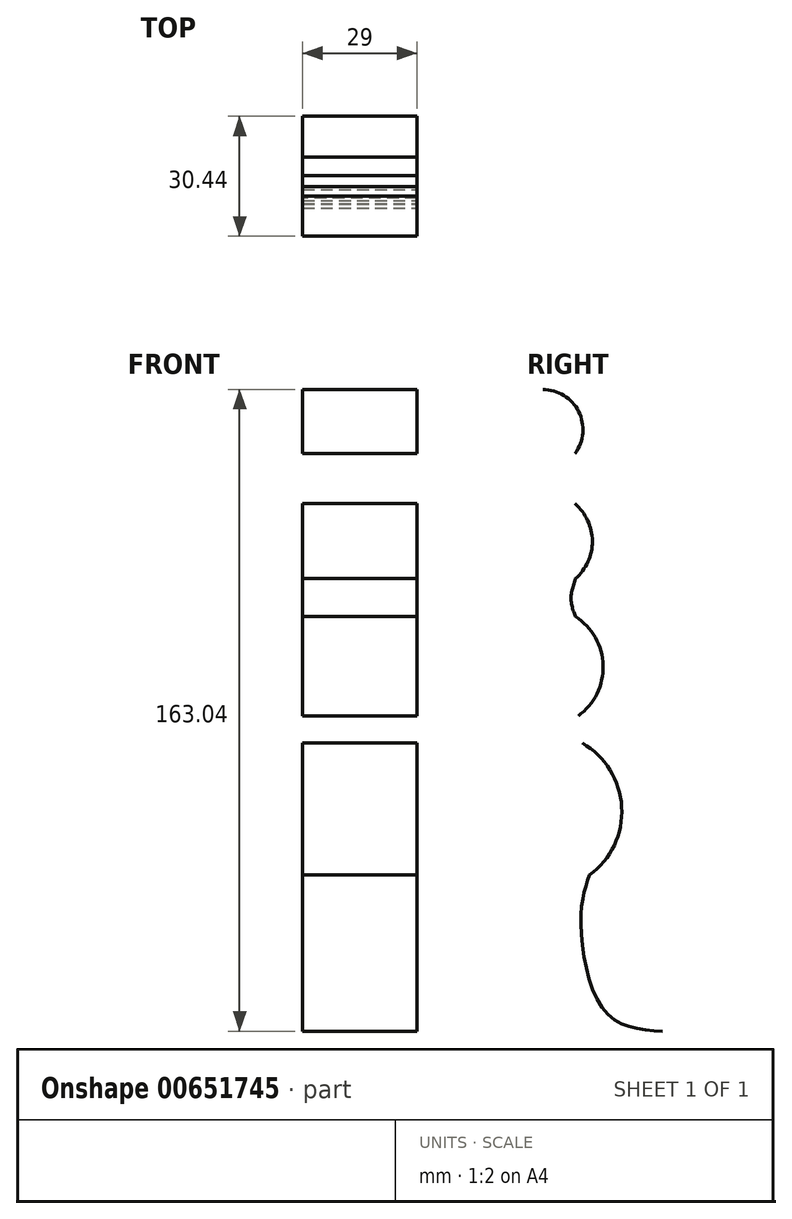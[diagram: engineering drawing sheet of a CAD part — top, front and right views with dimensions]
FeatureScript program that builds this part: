
annotation { "Feature Type Name" : "Feature", "Feature Type Description" : "" }
export const myFeature = defineFeature(function(context is Context, id is Id, definition is map)
    precondition{}
    {
        {
            var Q0;
            Q0=qCreatedBy(makeId("Right.planeOp"),FACE);
            var sketch = newSketch(context, id + "F0", { "sketchPlane" : qUnion([Q0])});
            skLineSegment(sketch, "E0", {"start": v(0, 0) * mm, "end": v(0, 163) * mm});
            skArc(sketch, "E1", {"start": v(8.28, 114.98) * mm, "mid": v(12.57, 124.54) * mm, "end": v(8.13, 134.03) * mm});
            skArc(sketch, "E2", {"start": v(9, 80.1) * mm, "mid": v(15.3, 92.93) * mm, "end": v(8.28, 105.37) * mm});
            skArc(sketch, "E3", {"start": v(11.86, 39.67) * mm, "mid": v(20.02, 56.94) * mm, "end": v(10.02, 73.22) * mm});
            skLineSegment(sketch, "E4", {"start": v(0, 0) * mm, "end": v(0, -5.25) * mm});
            skLineSegment(sketch, "E5", {"start": v(0, -5.25) * mm, "end": v(30.44, -5.25) * mm});
            skLineSegment(sketch, "E6", {"start": v(30.44, -5.25) * mm, "end": v(30.44, 0) * mm});
            skArc(sketch, "E7", {"start": v(8.2, 146.83) * mm, "mid": v(9.08, 157.46) * mm, "end": v(0, 163.04) * mm});
            skLineSegment(sketch, "E8", {"start": v(0, 163) * mm, "end": v(0, 163.04) * mm});
            skFitSpline(sketch, "E9", {"points": [v(8.2, 146.83) * mm, v(6.31, 140.52) * mm, v(8.28, 133.9) * mm, v(8.13, 134.03) * mm], "startDerivative": vector(-7.16, -11.87) * mm, "endDerivative": vector(-2.45, 2.92) * mm});
            skFitSpline(sketch, "E10", {"points": [v(8.28, 114.98) * mm, v(7.14, 109.9) * mm, v(8.28, 105.37) * mm], "startDerivative": vector(-3.38, -10.03) * mm, "endDerivative": vector(3.44, -9.19) * mm});
            skFitSpline(sketch, "E11", {"points": [v(9, 80.1) * mm, v(8.58, 77.22) * mm, v(10.07, 73.2) * mm, v(10.17, 73.52) * mm], "startDerivative": vector(-2.33, -6.04) * mm, "endDerivative": vector(0.33, 3.8) * mm});
            skFitSpline(sketch, "E12", {"points": [v(11.86, 39.67) * mm, v(9.7, 29.32) * mm, v(15.86, 4.96) * mm, v(30.44, 0) * mm], "startDerivative": vector(-11.2, -31.81) * mm, "endDerivative": vector(50.86, -3.42) * mm});
            skSolve(sketch);
        }
        {
            var Q0;
            Q0=makeQuery(id+"F0.imprint","IMPRINT",FACE,{"disambiguationData":[TD([[makeQuery(id+"F0.imprint","IMPRINT",EDGE,{"derivedFrom":sQuery(id+"F0.wireOp",EDGE,"E0")}),-1.0]])]});
            var Q1;
            Q1=sQuery(id+"F0.wireOp",EDGE,"E12");
            var Q2;
            Q2=sQuery(id+"F0.wireOp",EDGE,"E3");
            var Q3;
            Q3=sQuery(id+"F0.wireOp",EDGE,"E2");
            var Q4;
            Q4=sQuery(id+"F0.wireOp",EDGE,"E1");
            var Q5;
            Q5=sQuery(id+"F0.wireOp",EDGE,"E7");
            var Q6;
            Q6=sQuery(id+"F0.wireOp",EDGE,"E10");
            extrude(context, id + "F1", {"entities" : qUnion([Q0]), "bodyType" : ToolBodyType.SURFACE, "operationType" : NewBodyOperationType.INTERSECT, "surfaceEntities" : qUnion([Q1, Q2, Q3, Q4, Q5, Q6]), "depth" : 29 * mm, "offsetDistance" : 25 * mm});
        }
    });
